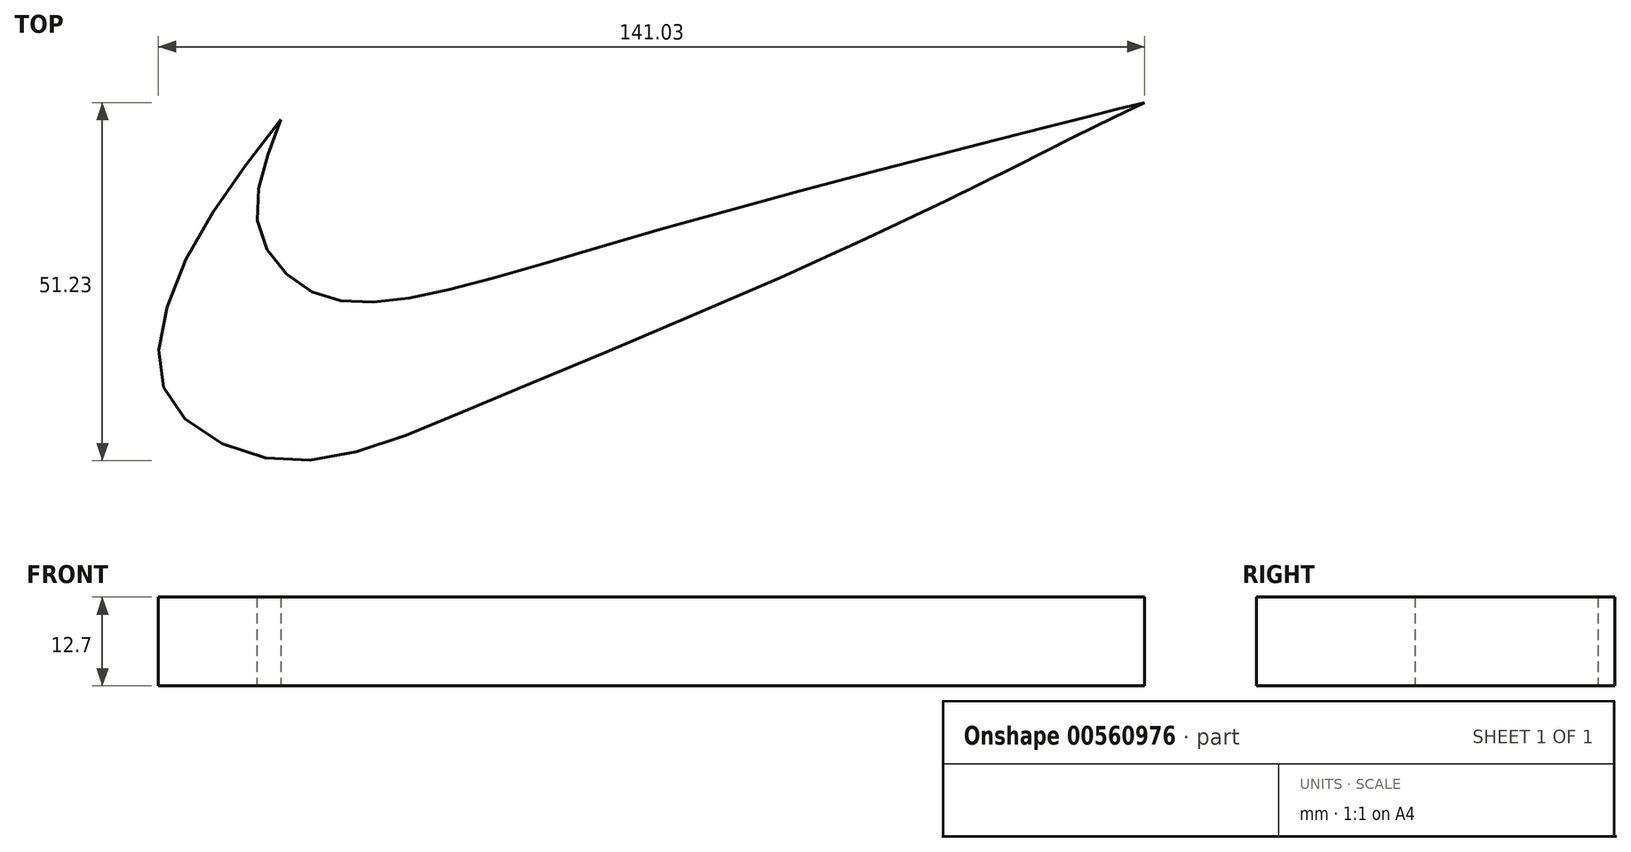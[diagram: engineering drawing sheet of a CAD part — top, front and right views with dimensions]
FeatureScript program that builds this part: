
annotation { "Feature Type Name" : "Feature", "Feature Type Description" : "" }
export const myFeature = defineFeature(function(context is Context, id is Id, definition is map)
    precondition{}
    {
        {
            var Q0;
            Q0=qCreatedBy(makeId("Top.planeOp"),FACE);
            var sketch = newSketch(context, id + "F0", { "sketchPlane" : qUnion([Q0])});
            skFitSpline(sketch, "E0", {"points": [v(-41.88, 5.07) * mm, v(-54.25, -12.57) * mm, v(-59.32, -27.38) * mm, v(-57.1, -36.1) * mm, v(-46.14, -42.87) * mm, v(-32.75, -42.87) * mm, v(-11.46, -34.88) * mm, v(37.42, -14) * mm, v(72.91, 3.25) * mm, v(81.63, 7.5) * mm], "startDerivative": vector(-118.33, -151.46) * mm, "endDerivative": vector(95.15, 45.76) * mm});
            skFitSpline(sketch, "E1", {"points": [v(81.63, 7.5) * mm, v(67.03, 3.85) * mm, v(9.23, -11.56) * mm, v(-23.83, -20.48) * mm, v(-37.62, -19.47) * mm, v(-45.13, -10.14) * mm, v(-41.88, 5.07) * mm], "startDerivative": vector(-85.81, -21.18) * mm, "endDerivative": vector(45.09, 115.36) * mm});
            skSolve(sketch);
        }
        {
            var Q0;
            Q0=makeQuery(id+"F0.imprint","IMPRINT",FACE,{"disambiguationData":[TD([[makeQuery(id+"F0.imprint","IMPRINT",EDGE,{"derivedFrom":sQuery(id+"F0.wireOp",EDGE,"E0")}),1.0]])]});
            extrude(context, id + "F1", {"entities" : qUnion([Q0]), "depth" : 12.7 * mm, "offsetDistance" : 25.4 * mm});
        }
    });
